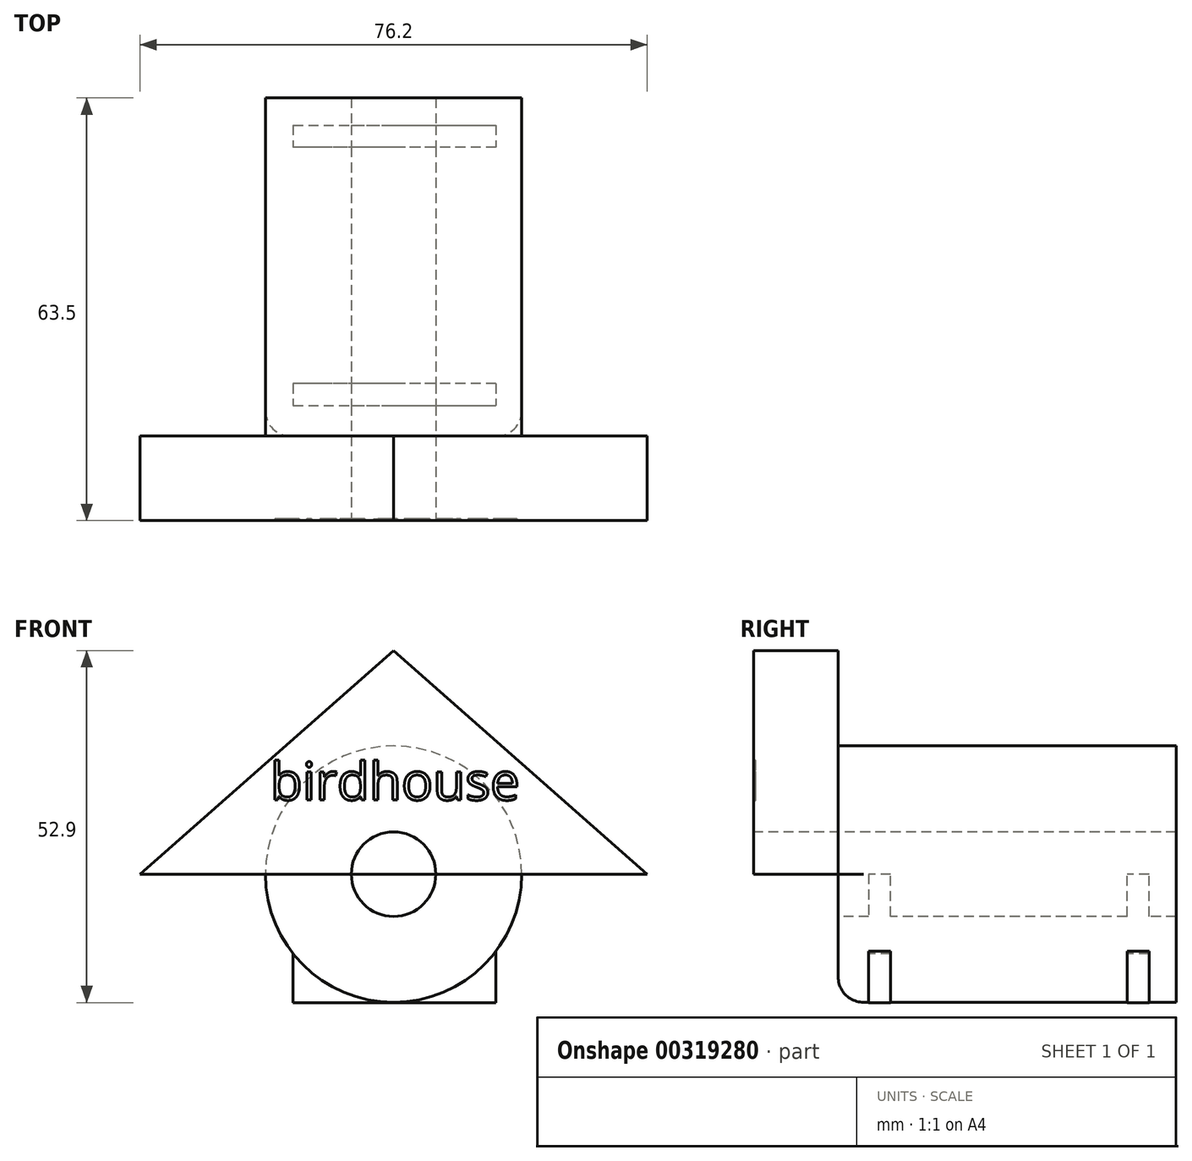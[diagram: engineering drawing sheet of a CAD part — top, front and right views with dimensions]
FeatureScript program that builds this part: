
annotation { "Feature Type Name" : "Feature", "Feature Type Description" : "" }
export const myFeature = defineFeature(function(context is Context, id is Id, definition is map)
    precondition{}
    {
        {
            var Q0;
            Q0=qCreatedBy(makeId("Front.planeOp"),FACE);
            var sketch = newSketch(context, id + "F0", { "sketchPlane" : qUnion([Q0])});
            skLineSegment(sketch, "E0", {"start": v(0, 0) * mm, "end": v(38.1, 0) * mm});
            skLineSegment(sketch, "E1", {"start": v(38.1, 0) * mm, "end": v(0, 33.6) * mm});
            skLineSegment(sketch, "E2", {"start": v(0, 33.6) * mm, "end": v(-38.1, 0) * mm});
            skLineSegment(sketch, "E3", {"start": v(-38.1, 0) * mm, "end": v(0, 0) * mm});
            skSolve(sketch);
        }
        {
            var Q0;
            Q0 = qSketchRegion(id + "F0", true);
            extrude(context, id + "F1", {"entities" : qUnion([Q0]), "depth" : 12.7 * mm});
        }
        {
            var Q0;
            Q0=qCreatedBy(makeId("Top.planeOp"),FACE);
            var sketch = newSketch(context, id + "F2", { "sketchPlane" : qUnion([Q0])});
            skLineSegment(sketch, "E4", {"start": v(0, 50.8) * mm, "end": v(19.25, 50.8) * mm});
            skLineSegment(sketch, "E5", {"start": v(19.25, 50.8) * mm, "end": v(19.25, 0) * mm});
            skLineSegment(sketch, "E6", {"start": v(19.25, 0) * mm, "end": v(0, 0) * mm});
            skLineSegment(sketch, "E7", {"start": v(0, 0) * mm, "end": v(0, 50.8) * mm});
            skSolve(sketch);
        }
        {
            var Q0;
            Q0 = qSketchRegion(id + "F2", true);
            var Q1;
            Q1=sQuery(id+"F2.wireOp",EDGE,"E7");
            revolve(context, id + "F3", {"operationType" : NewBodyOperationType.ADD, "entities" : qUnion([Q0]), "axis" : qUnion([Q1]), "revolveType" : RevolveType.FULL});
        }
        {
            var Q0;
            Q0=qCreatedBy(makeId("Front.planeOp"),FACE);
            var sketch = newSketch(context, id + "F4", { "sketchPlane" : qUnion([Q0])});
            skCircle(sketch, "E8", {"center": v(0, 0) * mm, "radius": 6.35 * mm});
            skSolve(sketch);
        }
        {
            var Q0;
            Q0 = qSketchRegion(id + "F4", true);
            extrude(context, id + "F5", {"entities" : qUnion([Q0]), "operationType" : NewBodyOperationType.REMOVE, "endBound" : BoundingType.SYMMETRIC, "oppositeDirection" : true, "depth" : 105.16 * mm});
        }
        {
            var Q0;
            {var subQ0=sQuery(id+"F2.wireOp",EDGE,"E5");Q0=makeQuery(id+"F3.boolean.opBoolean","SPLIT",EDGE,{"disambiguationData":[topologyDisambiguationEdgeConnected([makeQuery(id+"F1.opExtrude","CAP_FACE",FACE,{"disambiguationData":[OSD([sQuery(id+"F0.wireOp",EDGE,"E0"),sQuery(id+"F0.wireOp",EDGE,"E1"),sQuery(id+"F0.wireOp",EDGE,"E2"),sQuery(id+"F0.wireOp",EDGE,"E3")])],"isStart":true})])],"derivedFrom":makeQuery(id+"F3.opRevolve","SWEPT_EDGE",EDGE,{"disambiguationData":[OSD([subQ0,sQuery(id+"F2.wireOp",EDGE,"E6")])]})});}
            fillet(context, id + "F6", {"entities" : qUnion([Q0]), "radius" : 3.8 * mm, "tangentPropagation" : true, "allowEdgeOverflow" : false});
        }
        {
            var Q0;
            Q0=makeQuery(id+"F1.opExtrude","CAP_FACE",FACE,{"disambiguationData":[OSD([sQuery(id+"F0.wireOp",EDGE,"E0"),sQuery(id+"F0.wireOp",EDGE,"E1"),sQuery(id+"F0.wireOp",EDGE,"E2"),sQuery(id+"F0.wireOp",EDGE,"E3")])],"isStart":false});
            var sketch = newSketch(context, id + "F7", { "sketchPlane" : qUnion([Q0])});
            skText(sketch, "E9", { "text": "birdhouse", "fontName": "OpenSans-Regular.ttf"});
            const initialGuessF7  = {"E9": [-0.01852, 0.01113, 1, 0, 0.00567]};
            skSetInitialGuess(sketch, initialGuessF7);
            skSolve(sketch);
        }
        {
            var Q0;
            Q0 = qSketchRegion(id + "F7", true);
            extrude(context, id + "F8", {"entities" : qUnion([Q0]), "operationType" : NewBodyOperationType.REMOVE, "oppositeDirection" : true, "depth" : 0.25 * mm});
        }
        {
            var Q0;
            Q0=qCreatedBy(makeId("Top.planeOp"),FACE);
            var sketch = newSketch(context, id + "F9", { "sketchPlane" : qUnion([Q0])});
            skLineSegment(sketch, "E10", {"start": v(-15.09, 4.6) * mm, "end": v(15.4, 4.6) * mm});
            skLineSegment(sketch, "E11", {"start": v(15.4, 4.6) * mm, "end": v(15.4, 7.9) * mm});
            skLineSegment(sketch, "E12", {"start": v(15.4, 7.9) * mm, "end": v(-15.09, 7.9) * mm});
            skLineSegment(sketch, "E13", {"start": v(-15.09, 7.9) * mm, "end": v(-15.09, 4.6) * mm});
            skLineSegment(sketch, "E14", {"start": v(-15.09, 46.71) * mm, "end": v(15.4, 46.71) * mm});
            skLineSegment(sketch, "E15", {"start": v(15.4, 46.71) * mm, "end": v(15.4, 43.41) * mm});
            skLineSegment(sketch, "E16", {"start": v(15.4, 43.41) * mm, "end": v(-15.09, 43.41) * mm});
            skLineSegment(sketch, "E17", {"start": v(-15.09, 46.71) * mm, "end": v(-15.09, 43.41) * mm});
            skSolve(sketch);
        }
        {
            var Q0;
            Q0 = qSketchRegion(id + "F9", true);
            extrude(context, id + "F10", {"entities" : qUnion([Q0]), "operationType" : NewBodyOperationType.ADD, "oppositeDirection" : true, "depth" : 19.3 * mm});
        }
    });
